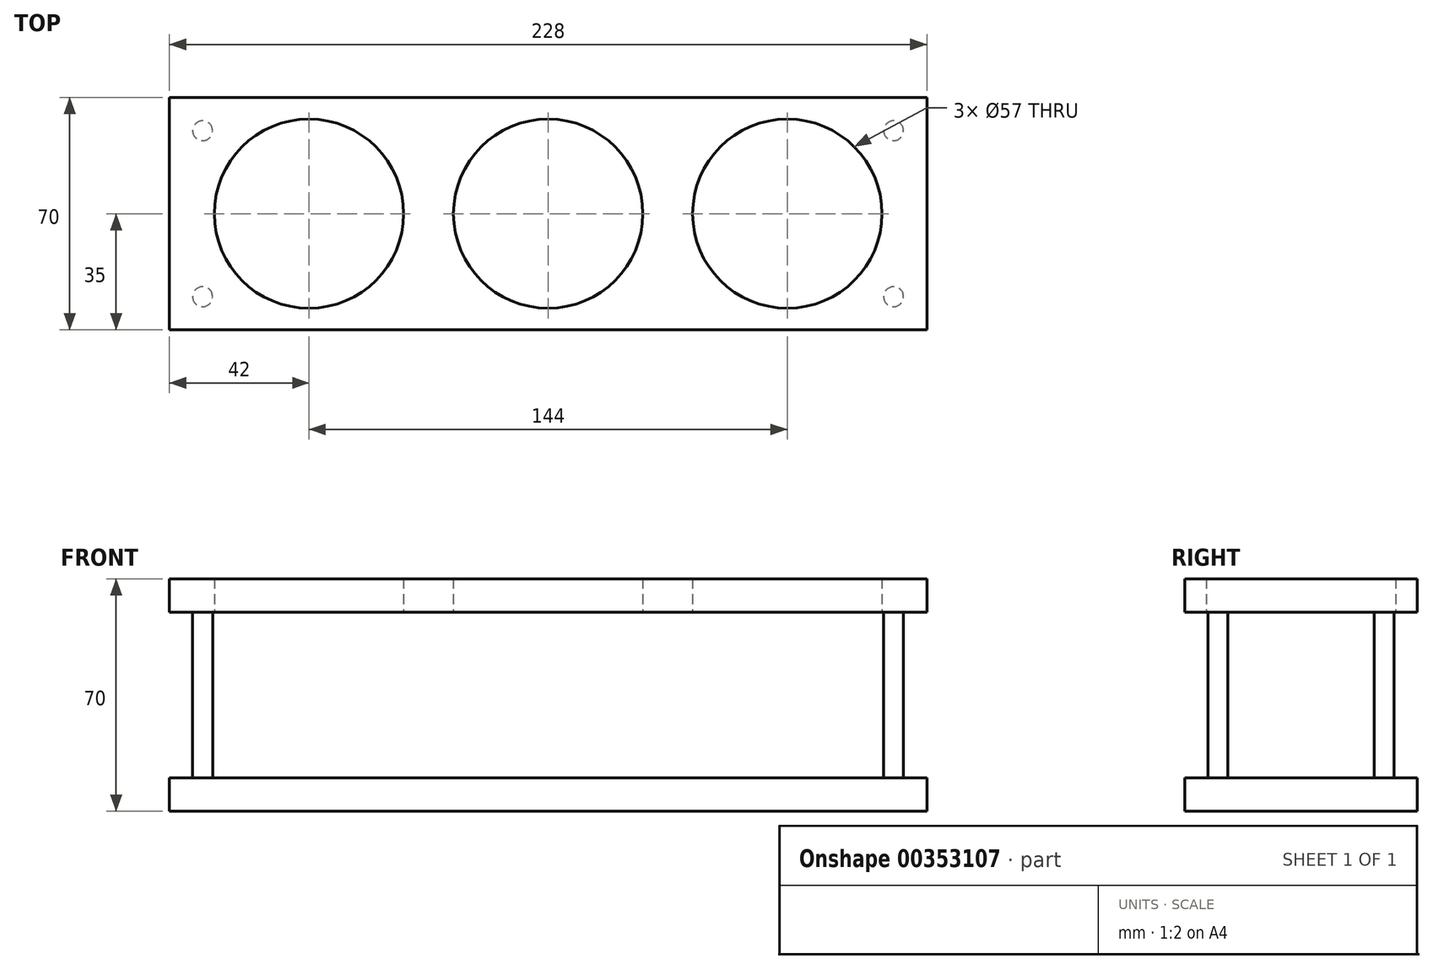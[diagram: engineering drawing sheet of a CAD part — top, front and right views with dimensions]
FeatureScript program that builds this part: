
annotation { "Feature Type Name" : "Feature", "Feature Type Description" : "" }
export const myFeature = defineFeature(function(context is Context, id is Id, definition is map)
    precondition{}
    {
        {
            var Q0;
            Q0=qCreatedBy(makeId("Top.planeOp"),FACE);
            var sketch = newSketch(context, id + "F0", { "sketchPlane" : qUnion([Q0])});
            skLineSegment(sketch, "E0.bottom", {"start": v(114, -35) * mm, "end": v(-114, -35) * mm});
            skLineSegment(sketch, "E0.top", {"start": v(114, 35) * mm, "end": v(-114, 35) * mm});
            skLineSegment(sketch, "E0.left", {"start": v(114, -35) * mm, "end": v(114, 35) * mm});
            skLineSegment(sketch, "E0.right", {"start": v(-114, -35) * mm, "end": v(-114, 35) * mm});
            skPoint(sketch, "E0.middle", {"position": v(0, 0) * mm});
            skSolve(sketch);
        }
        {
            var Q0;
            Q0=qSketchRegion(id+"F0",true);
            extrude(context, id + "F1", {"entities" : qUnion([Q0]), "depth" : 10 * mm});
        }
        {
            var Q0;
            Q0=makeQuery(id+"F1.opExtrude","CAP_FACE",FACE,{"disambiguationData":[OSD([sQuery(id+"F0.wireOp",EDGE,"E0.bottom"),sQuery(id+"F0.wireOp",EDGE,"E0.top"),sQuery(id+"F0.wireOp",EDGE,"E0.left"),sQuery(id+"F0.wireOp",EDGE,"E0.right")])],"isStart":false});
            cPlane(context, id + "F2", {"entities" : qUnion([Q0]), "cplaneType" : CPlaneType.OFFSET, "offset" : 50 * mm, "width" : 150 * mm, "height" : 150 * mm});
        }
        {
            var Q0;
            Q0=qCreatedBy(id+"F2.planeOp",FACE);
            var sketch = newSketch(context, id + "F3", { "sketchPlane" : qUnion([Q0])});
            skLineSegment(sketch, "E1.0", {"start": v(114, -35) * mm, "end": v(-114, -35) * mm});
            skLineSegment(sketch, "E1.1", {"start": v(114, 35) * mm, "end": v(-114, 35) * mm});
            skLineSegment(sketch, "E1.2", {"start": v(114, -35) * mm, "end": v(114, 35) * mm});
            skLineSegment(sketch, "E1.3", {"start": v(-114, -35) * mm, "end": v(-114, 35) * mm});
            skPoint(sketch, "E1.4", {"position": v(0, 0) * mm});
            skLineSegment(sketch, "E2", {"start": v(-114, 0) * mm, "end": v(114, 0) * mm, "construction": true});
            skCircle(sketch, "E3", {"center": v(-72, 0) * mm, "radius": 28.5 * mm});
            skCircle(sketch, "E4.1.0.0", {"center": v(0, 0) * mm, "radius": 28.5 * mm});
            skCircle(sketch, "E4.2.0.0", {"center": v(72, 0) * mm, "radius": 28.5 * mm});
            skLineSegment(sketch, "E4.direction1", {"start": v(-72, 0) * mm, "end": v(0, 0) * mm, "construction": true});
            skSolve(sketch);
        }
        {
            var Q0;
            Q0=qSketchRegion(id+"F3",true);
            extrude(context, id + "F4", {"entities" : qUnion([Q0]), "depth" : 10 * mm});
        }
        {
            var Q0;
            Q0=makeQuery(id+"F1.opExtrude","CAP_FACE",FACE,{"disambiguationData":[OSD([sQuery(id+"F0.wireOp",EDGE,"E0.bottom"),sQuery(id+"F0.wireOp",EDGE,"E0.top"),sQuery(id+"F0.wireOp",EDGE,"E0.left"),sQuery(id+"F0.wireOp",EDGE,"E0.right")])],"isStart":false});
            var sketch = newSketch(context, id + "F5", { "sketchPlane" : qUnion([Q0])});
            skLineSegment(sketch, "E5", {"start": v(-114, 0) * mm, "end": v(114, 0) * mm, "construction": true});
            skLineSegment(sketch, "E6", {"start": v(114, 0) * mm, "end": v(0, 0) * mm, "construction": true});
            skLineSegment(sketch, "E7", {"start": v(0, 0) * mm, "end": v(0, 35) * mm, "construction": true});
            skCircle(sketch, "E8", {"center": v(-104, -25) * mm, "radius": 3 * mm});
            skCircle(sketch, "E9.MirrorC", {"center": v(-104, 25) * mm, "radius": 3 * mm});
            skCircle(sketch, "E10.MirrorC", {"center": v(104, 25) * mm, "radius": 3 * mm});
            skCircle(sketch, "E11.MirrorC", {"center": v(104, -25) * mm, "radius": 3 * mm});
            skSolve(sketch);
        }
        {
            var Q0;
            Q0=qSketchRegion(id+"F5",true);
            var Q1;
            Q1=makeQuery(id+"F4.opExtrude","CAP_FACE",FACE,{"disambiguationData":[OSD([sQuery(id+"F3.wireOp",EDGE,"E1.0"),sQuery(id+"F3.wireOp",EDGE,"E1.1"),sQuery(id+"F3.wireOp",EDGE,"E1.2"),sQuery(id+"F3.wireOp",EDGE,"E1.3"),sQuery(id+"F3.wireOp",EDGE,"E3"),sQuery(id+"F3.wireOp",EDGE,"E4.1.0.0"),sQuery(id+"F3.wireOp",EDGE,"E4.2.0.0"),sQuery(id+"F3.wireOp",EDGE,"E4.3.0.0")])],"isStart":true});
            extrude(context, id + "F6", {"entities" : qUnion([Q0]), "endBound" : BoundingType.UP_TO_SURFACE, "endBoundEntityFace" : qUnion([Q1]), "depth" : 25 * mm});
        }
    });
